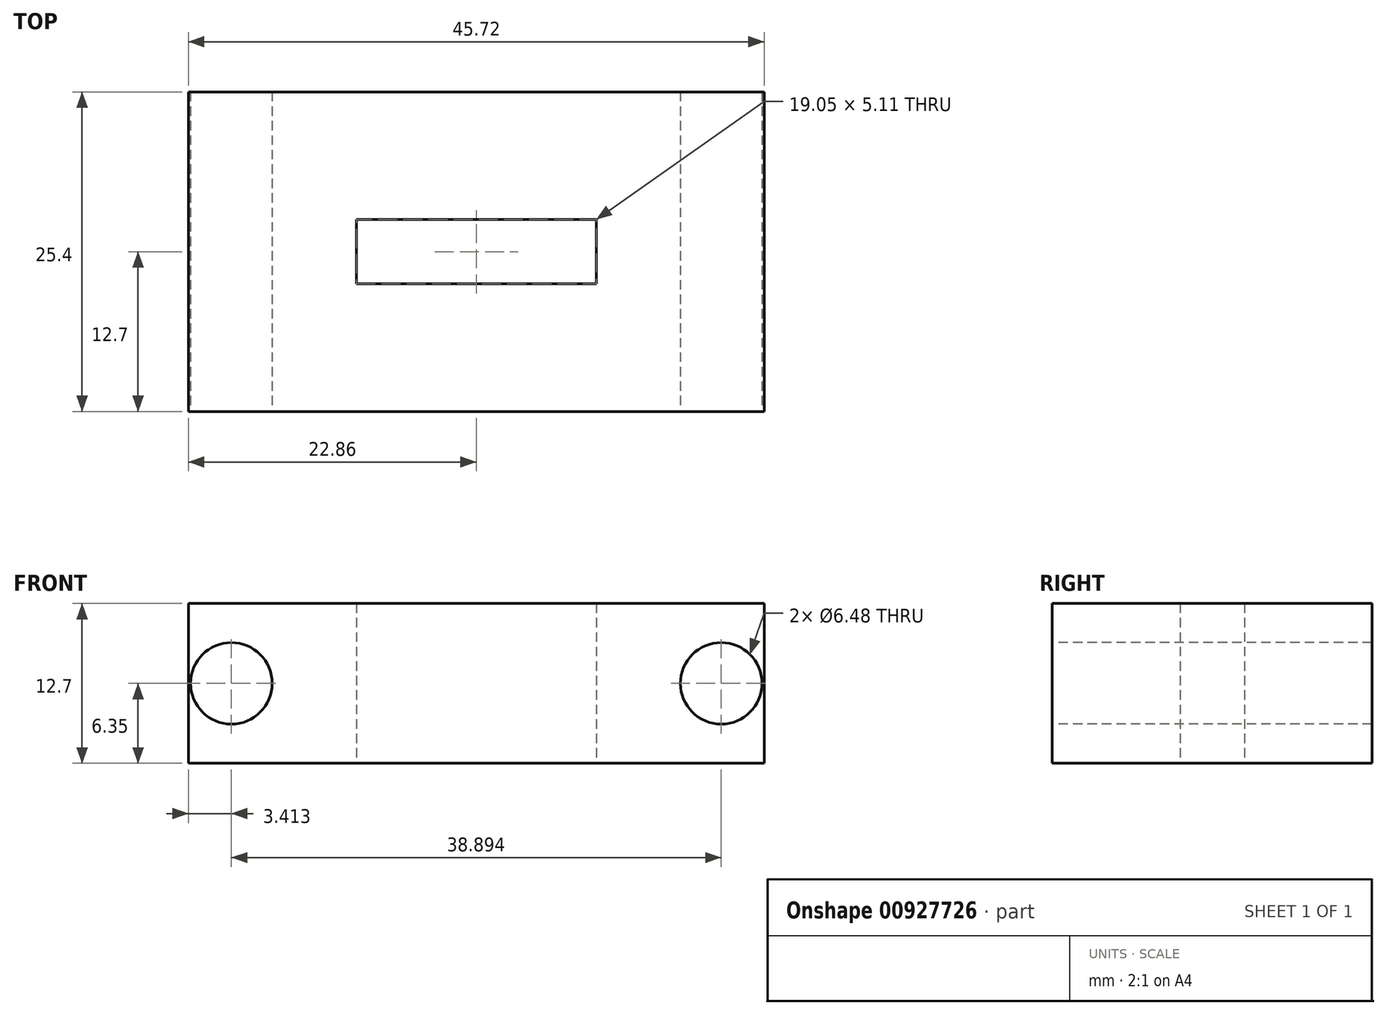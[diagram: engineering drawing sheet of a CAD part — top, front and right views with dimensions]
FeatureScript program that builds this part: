
annotation { "Feature Type Name" : "Feature", "Feature Type Description" : "" }
export const myFeature = defineFeature(function(context is Context, id is Id, definition is map)
    precondition{}
    {
        {
            var Q0;
            Q0=qCreatedBy(makeId("Top.planeOp"),FACE);
            var sketch = newSketch(context, id + "F0", { "sketchPlane" : qUnion([Q0])});
            skLineSegment(sketch, "E0.bottom", {"start": v(22.86, 12.7) * mm, "end": v(-22.86, 12.7) * mm});
            skLineSegment(sketch, "E0.top", {"start": v(22.86, -12.7) * mm, "end": v(-22.86, -12.7) * mm});
            skLineSegment(sketch, "E0.left", {"start": v(22.86, 12.7) * mm, "end": v(22.86, -12.7) * mm});
            skLineSegment(sketch, "E0.right", {"start": v(-22.86, 12.7) * mm, "end": v(-22.86, -12.7) * mm});
            skPoint(sketch, "E0.middle", {"position": v(0, 0) * mm});
            skLineSegment(sketch, "E1.bottom", {"start": v(9.53, -2.55) * mm, "end": v(-9.53, -2.55) * mm});
            skLineSegment(sketch, "E1.top", {"start": v(9.53, 2.55) * mm, "end": v(-9.53, 2.55) * mm});
            skLineSegment(sketch, "E1.left", {"start": v(9.53, -2.55) * mm, "end": v(9.53, 2.55) * mm});
            skLineSegment(sketch, "E1.right", {"start": v(-9.53, -2.55) * mm, "end": v(-9.53, 2.55) * mm});
            skSolve(sketch);
        }
        {
            var Q0;
            Q0=makeQuery(id+"F0.imprint","IMPRINT",FACE,{"disambiguationData":[TD([[makeQuery(id+"F0.imprint","IMPRINT",EDGE,{"derivedFrom":sQuery(id+"F0.wireOp",EDGE,"E0.bottom")}),1.0]])]});
            extrude(context, id + "F1", {"entities" : qUnion([Q0]), "depth" : 12.7 * mm, "offsetDistance" : 25.4 * mm});
        }
        {
            var Q0;
            Q0=makeQuery(id+"F1.opExtrude","SWEPT_FACE",FACE,{"disambiguationData":[OSD([sQuery(id+"F0.wireOp",EDGE,"E0.top")])]});
            var sketch = newSketch(context, id + "F2", { "sketchPlane" : qUnion([Q0])});
            skPoint(sketch, "E2", {"position": v(-19.45, 6.35) * mm});
            skPoint(sketch, "E3", {"position": v(19.45, 6.35) * mm});
            skSolve(sketch);
        }
        {
            var Q0;
            Q0=sQuery(id+"F2.wireOp",VERTEX,"E2");
            var Q1;
            Q1=sQuery(id+"F2.wireOp",VERTEX,"E3");
            var Q2;
            Q2=makeQuery(id+"F1.opExtrude","SWEPT_BODY",BODY,{"disambiguationData":[OSD([sQuery(id+"F0.wireOp",EDGE,"E0.bottom"),sQuery(id+"F0.wireOp",EDGE,"E0.top"),sQuery(id+"F0.wireOp",EDGE,"E0.left"),sQuery(id+"F0.wireOp",EDGE,"E0.right")])]});
            hole(context, id + "F3", {"style" : HoleStyle.SIMPLE, "endStyle" : HoleEndStyle.THROUGH, "holeDiameter" : 6.48 * mm, "majorDiameter" : 6.35 * mm, "isTappedThrough" : true, "tappedDepth" : 12.7 * mm, "tapClearance" : 3, "locations" : qUnion([Q0, Q1]), "scope" : qUnion([Q2])});
        }
    });
